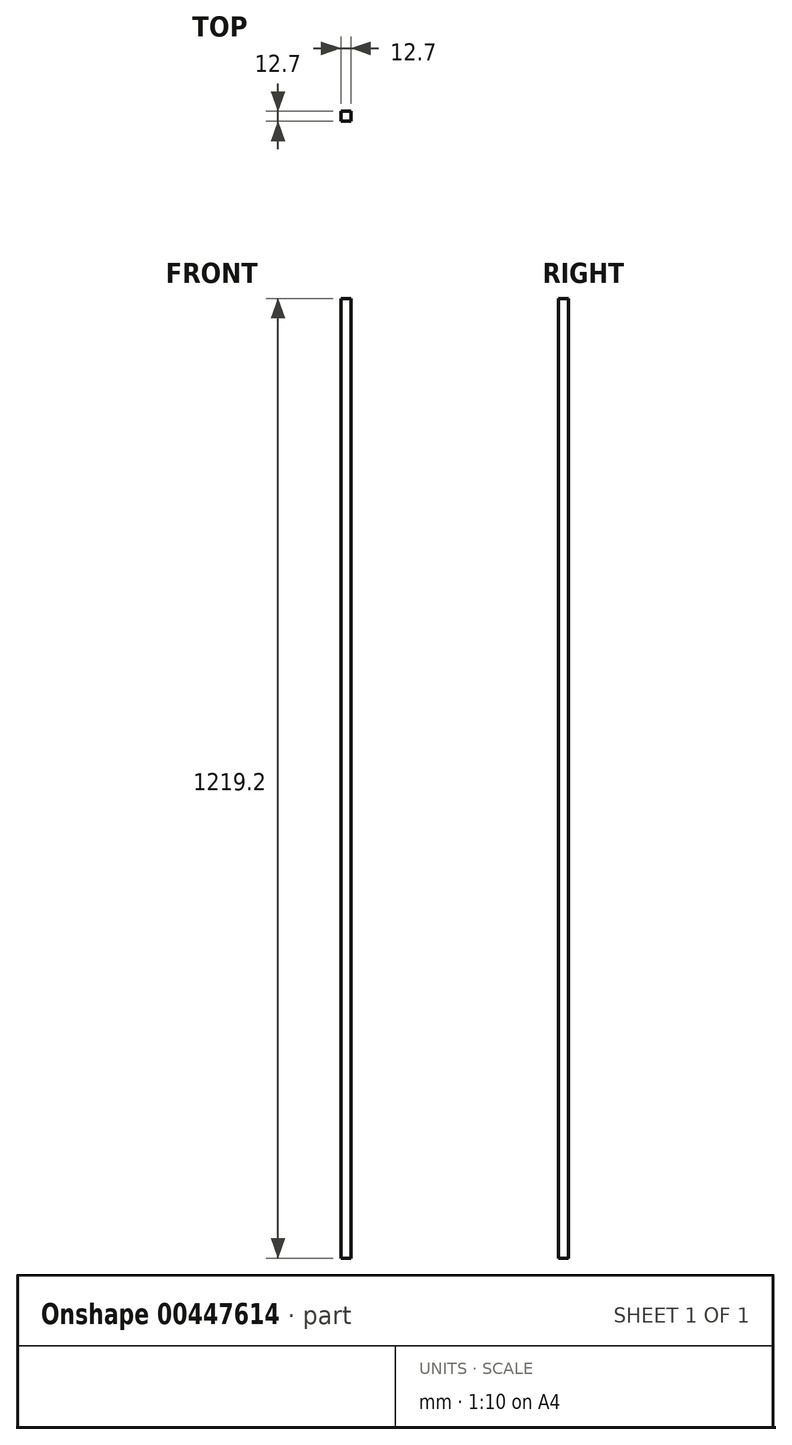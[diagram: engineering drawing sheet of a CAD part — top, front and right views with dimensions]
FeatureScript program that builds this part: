
annotation { "Feature Type Name" : "Feature", "Feature Type Description" : "" }
export const myFeature = defineFeature(function(context is Context, id is Id, definition is map)
    precondition{}
    {
        {
            var Q0;
            Q0=qCreatedBy(makeId("Front.planeOp"),FACE);
            var sketch = newSketch(context, id + "F0", { "sketchPlane" : qUnion([Q0])});
            skLineSegment(sketch, "E0.bottom", {"start": v(0, 0) * mm, "end": v(12.7, 0) * mm});
            skLineSegment(sketch, "E0.top", {"start": v(0, -1219.2) * mm, "end": v(12.7, -1219.2) * mm});
            skLineSegment(sketch, "E0.left", {"start": v(0, 0) * mm, "end": v(0, -1219.2) * mm});
            skLineSegment(sketch, "E0.right", {"start": v(12.7, 0) * mm, "end": v(12.7, -1219.2) * mm});
            skSolve(sketch);
        }
        {
            var Q0;
            Q0 = qSketchRegion(id + "F0", true);
            extrude(context, id + "F1", {"entities" : qUnion([Q0]), "depth" : 12.7 * mm});
        }
    });
